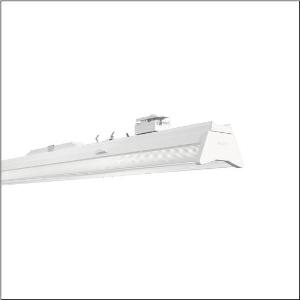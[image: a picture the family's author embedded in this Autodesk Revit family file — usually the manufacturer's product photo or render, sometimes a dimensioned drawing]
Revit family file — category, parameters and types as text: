
# Revit family: licross_r__11_performance_mo_51tm167n485g_4c90
name_source: partatom
category: Lighting Fixtures
units: mm (PartAtom-declared; Revit-internal decimal feet)

## family parameters
Cut with Voids When Loaded = No
Host = Face
Light Source = No
Part Type = Normal
Room Calculation Point = No
Round Connector Dimension = Use Diameter
Shared = No

## types (1)
- Licross® 11 Performance MO (1 x LED, 8840 lm, 48.6 W, 4000K)
    Apparent Load = 49 VA
    CIE Flux Codes = 66 88 96 79 100
    Color Rendering = 80
    Color Temperature = 4000K
    Default Elevation = 1800 mm
    Description = Licross® 11 Performance MO, luminaire insert, of sheet steel, galvanised, coil coated, white, length: 1.500mm, width: 120mm, height: 123mm, LED rated luminous flux: 8.840lm, light colour: 840, control gear: ON/OFF, with plug, 3-pole, with phase selection, mains connection: 220..240V, AC, 50/60Hz, rated input power: 49W, halogen-free wiring, primary light control with lens, of plastic, primary optical cover: cover, of PMMA, light emission: direct/indirect distribution, primary light characteristic: symmetric, protection rating (complete): IP40, insulation class (complete): insulation class I (protective earthing), certification: CE, ENEC, VDE, UKCA, protection symbol: D if used in an environment without relevant dust loads with corresponding accessories, impact resistance: IK06, permissible ambient temperature for indoor applications: -25..+35°C, corresponds to IFS (International Featured Standards) requirements for safety and quality in the food industry, reducing of maximum allowable ambient temperature of 5°C with ceiling mounting, LABS conformity tested according to VDMA 24364:2018-05, packaging unit: 1 piece
    Height = 114 mm
    Lamp = 1 x LED
    Lamp Light Flux = 8840 lm
    Lamp Power = 48.6 W
    Lamp count = 1
    Length = 1500 mm
    Luminous efficacy = 182 lm/W
    Manufacturer = Siteco
    ModVariant = No
    Model = 51TM167N485G
    Mounting Place = Ceiling
    Mounting Type = Pendant
    Number of Poles = 1
    OnlyDefault = Yes
    Power Factor = 1
    Product Name = Licross® 11 Performance MO
    Product group = luminaire insert
    ProductGroupID = 901
    Protection Class = Protection class I
    Protection Degree = IP 40
    RLX_Detail_Level = 1
    RLX_Emergency_Light_Flux = 0 lm
    RLX_Emergency_Type = 0
    RLX_Emergency_Type_DB = No
    RlxData = <blob elided: 30433 chars, md5=6c06138e>
    Socket = socket
    Standby Power = 0 W
    System Light Flux = 8840 lm
    System Power = 49 W
    Type Comments = Product without accessories
    Type Image = l_1256138.jpg
    URL = http://relux.com
    VarID = ---
    Voltage = 0 V
    Weight = 0.00 kg
    Width = 120 mm

## geometry (parser evidence)
native form markers: Blend x4, Sweep x15
no freeform markers — native parametric forms only
